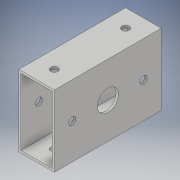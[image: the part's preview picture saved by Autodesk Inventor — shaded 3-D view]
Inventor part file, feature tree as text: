
AUTODESK INVENTOR PART (.ipt)
format: ipt  version: 2018 (Build 220112000, 112)  size: 140,800 bytes
history: native  units: in
note: dims shown in document units (in); Inventor stores cm internally (conversion verified against a paired STEP export)
features: extrude x4, sketch x4
ambient origin geometry x8: Origin, YZ Plane, XZ Plane, XY Plane, X Axis, Y Axis, Z Axis, Center Point
bodies: Solid1 (feature_tree)
feature tree (8):
  extrude  "Extrusion1"  Depth=2.0in
  extrude  "Extrusion3"  Depth=3.0in TaperAngle=0.0deg
  extrude  "Extrusion4"  Depth=1.0in TaperAngle=0.0deg
  extrude  "Extrusion5"  Depth=1.0in
  sketch  "Sketch1"  dims[d0=1.0in d1=2.0in]
  sketch  "Sketch3"  dims[d2=0.0625in d3=3.0in d4=0.0in]
  sketch  "Sketch4"  dims[d10=1.0in d12=3.25in d13=0.0in]
  sketch  "Sketch5"  dims[d15=0.59in d16=0.5in d17=0.5in d18=0.2031in d19=3.25in d20=0.0in d21=0.5in d22=0.5in d23=0.2031in d24=1.0in d25=0.0in]
